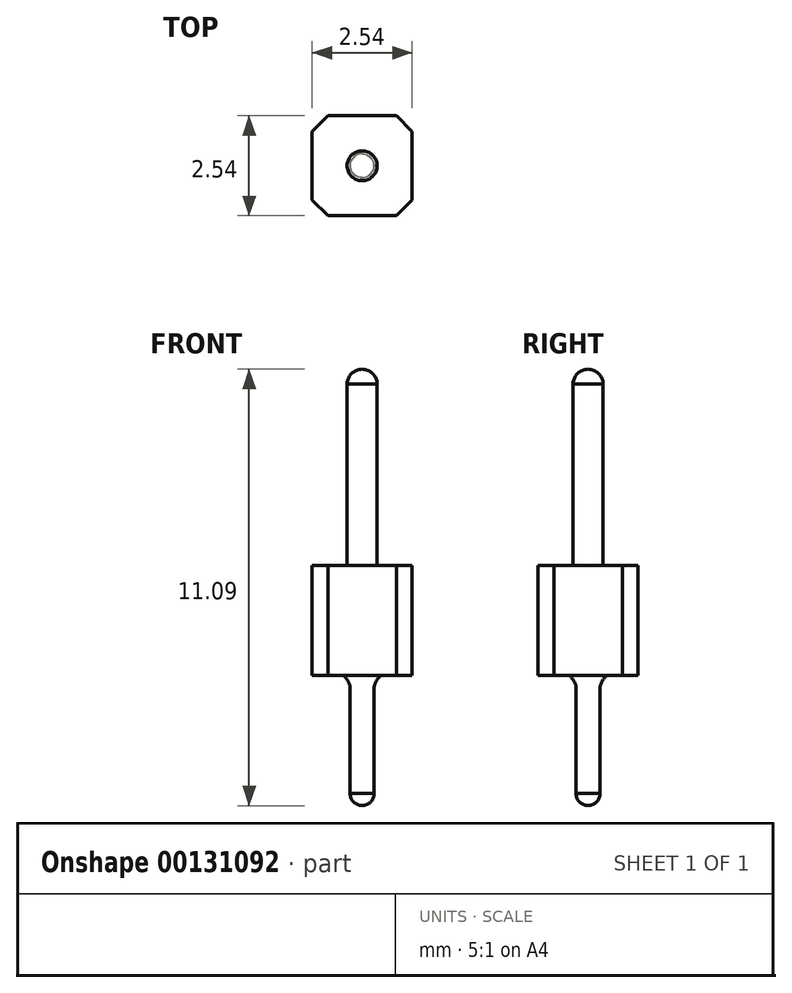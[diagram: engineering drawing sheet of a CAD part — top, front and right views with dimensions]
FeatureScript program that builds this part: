
annotation { "Feature Type Name" : "Feature", "Feature Type Description" : "" }
export const myFeature = defineFeature(function(context is Context, id is Id, definition is map)
    precondition{}
    {
        {
            var Q0;
            Q0=qCreatedBy(makeId("Top.planeOp"),FACE);
            var sketch = newSketch(context, id + "F0", { "sketchPlane" : qUnion([Q0])});
            skLineSegment(sketch, "E0", {"start": v(0, 0) * mm, "end": v(-1.27, 0) * mm});
            skCircle(sketch, "E1", {"center": v(-1.27, 0) * mm, "radius": 0.3 * mm});
            skSolve(sketch);
        }
        {
            var Q0;
            Q0=makeQuery(id+"F0.imprint","IMPRINT",FACE,{"disambiguationData":[TD([[makeQuery(id+"F0.imprint","IMPRINT",EDGE,{"derivedFrom":sQuery(id+"F0.wireOp",EDGE,"E1")}),1.0]])]});
            extrude(context, id + "F1", {"entities" : qUnion([Q0]), "oppositeDirection" : true, "depth" : 11.1 * mm, "hasSecondDirection" : true, "secondDirectionOppositeDirection" : true, "secondDirectionDepth" : 7.8 * mm});
        }
        {
            var Q0;
            Q0=makeQuery(id+"F1.opExtrude","CAP_FACE",FACE,{"disambiguationData":[OSD([sQuery(id+"F0.wireOp",EDGE,"E1")])],"isStart":false});
            extrude(context, id + "F2", {"entities" : qUnion([Q0]), "operationType" : NewBodyOperationType.REMOVE, "oppositeDirection" : true, "depth" : 0.3 * mm});
        }
        {
            var Q0;
            Q0=qCreatedBy(makeId("Top.planeOp"),FACE);
            var sketch = newSketch(context, id + "F3", { "sketchPlane" : qUnion([Q0])});
            skLineSegment(sketch, "E2", {"start": v(0, 0) * mm, "end": v(-1.27, 0) * mm});
            skCircle(sketch, "E3", {"center": v(-1.27, 0) * mm, "radius": 0.3 * mm});
            skLineSegment(sketch, "E4", {"start": v(-1.27, 0) * mm, "end": v(-1.8, 0) * mm});
            skSolve(sketch);
        }
        {
            var Q0;
            {var subQ0=sQuery(id+"F3.wireOp",EDGE,"E4");var subQ1=sQuery(id+"F3.wireOp",EDGE,"E2");var subQ2=makeQuery(id+"F3.imprint","INTERSECT",VERTEX,{"derivedFrom":[subQ1,subQ0]});Q0=makeQuery(id+"F3.imprint","IMPRINT",FACE,{"disambiguationData":[TD([[makeQuery(id+"F3.imprint","IMPRINT",EDGE,{"disambiguationData":[TD([[subQ2,1.0]])],"derivedFrom":subQ1}),-1.0]])]});}
            var Q1;
            Q1=sQuery(id+"F3.wireOp",EDGE,"E4");
            revolve(context, id + "F4", {"entities" : qUnion([Q0]), "axis" : qUnion([Q1]), "revolveType" : RevolveType.ONE_DIRECTION, "angle" : 180 * degree});
        }
        {
            var Q0;
            Q0=makeQuery(id+"F4.opRevolve","SWEPT_BODY",BODY,{"disambiguationData":[OSD([sQuery(id+"F3.wireOp",EDGE,"E2"),sQuery(id+"F3.wireOp",EDGE,"E3"),sQuery(id+"F3.wireOp",EDGE,"E4")])]});
            transform(context, id + "F5", {"entities" : qUnion([Q0]), "transformType" : TransformType.TRANSLATION_3D, "dx" : 0 * mm, "dy" : 0 * mm, "dz" : -10.8 * mm, "makeCopy" : false});
        }
        {
            var Q0;
            Q0=qCreatedBy(makeId("Top.planeOp"),FACE);
            var sketch = newSketch(context, id + "F6", { "sketchPlane" : qUnion([Q0])});
            skLineSegment(sketch, "E5", {"start": v(0, 0) * mm, "end": v(-1.27, 0) * mm});
            skLineSegment(sketch, "E6.bottom", {"start": v(0, 1.27) * mm, "end": v(-2.54, 1.27) * mm});
            skLineSegment(sketch, "E6.top", {"start": v(0, -1.27) * mm, "end": v(-2.54, -1.27) * mm});
            skLineSegment(sketch, "E6.left", {"start": v(0, 1.27) * mm, "end": v(0, -1.27) * mm});
            skLineSegment(sketch, "E6.right", {"start": v(-2.54, 1.27) * mm, "end": v(-2.54, -1.27) * mm});
            skPoint(sketch, "E6.middle", {"position": v(-1.27, 0) * mm});
            skSolve(sketch);
        }
        {
            var Q0;
            {var subQ3=sQuery(id+"F6.wireOp",EDGE,"E6.bottom");Q0=makeQuery(id+"F6.imprint","IMPRINT",FACE,{"disambiguationData":[TD([[makeQuery(id+"F6.imprint","IMPRINT",EDGE,{"derivedFrom":subQ3}),1.0]])]});}
            extrude(context, id + "F7", {"entities" : qUnion([Q0]), "oppositeDirection" : true, "depth" : 7.8 * mm, "hasSecondDirection" : true, "secondDirectionOppositeDirection" : true, "secondDirectionDepth" : 5 * mm});
        }
        {
            var Q0;
            Q0=qCreatedBy(makeId("Top.planeOp"),FACE);
            var sketch = newSketch(context, id + "F8", { "sketchPlane" : qUnion([Q0])});
            skLineSegment(sketch, "E7", {"start": v(0, 0) * mm, "end": v(-1.27, 0) * mm});
            skCircle(sketch, "E8", {"center": v(-1.27, 0) * mm, "radius": 0.38 * mm});
            skSolve(sketch);
        }
        {
            var Q0;
            Q0=makeQuery(id+"F8.imprint","IMPRINT",FACE,{"disambiguationData":[TD([[makeQuery(id+"F8.imprint","IMPRINT",EDGE,{"derivedFrom":sQuery(id+"F8.wireOp",EDGE,"E8")}),1.0]])]});
            extrude(context, id + "F9", {"entities" : qUnion([Q0]), "oppositeDirection" : true, "depth" : 5 * mm, "hasSecondDirection" : true, "secondDirectionOppositeDirection" : true, "secondDirectionDepth" : 0.4 * mm});
        }
        {
            var Q0;
            Q0=qCreatedBy(makeId("Top.planeOp"),FACE);
            var sketch = newSketch(context, id + "F10", { "sketchPlane" : qUnion([Q0])});
            skLineSegment(sketch, "E9", {"start": v(0, 0) * mm, "end": v(-1.27, 0) * mm});
            skCircle(sketch, "E10", {"center": v(-1.27, 0) * mm, "radius": 0.38 * mm});
            skLineSegment(sketch, "E11", {"start": v(-1.27, 0) * mm, "end": v(-1.76, 0) * mm});
            skSolve(sketch);
        }
        {
            var Q0;
            {var subQ0=sQuery(id+"F10.wireOp",EDGE,"E11");var subQ1=sQuery(id+"F10.wireOp",EDGE,"E9");var subQ2=makeQuery(id+"F10.imprint","INTERSECT",VERTEX,{"derivedFrom":[subQ1,subQ0]});Q0=makeQuery(id+"F10.imprint","IMPRINT",FACE,{"disambiguationData":[TD([[makeQuery(id+"F10.imprint","IMPRINT",EDGE,{"disambiguationData":[TD([[subQ2,1.0]])],"derivedFrom":subQ1}),-1.0]])]});}
            var Q1;
            Q1=sQuery(id+"F10.wireOp",EDGE,"E11");
            revolve(context, id + "F11", {"operationType" : NewBodyOperationType.ADD, "entities" : qUnion([Q0]), "axis" : qUnion([Q1]), "revolveType" : RevolveType.ONE_DIRECTION, "oppositeDirection" : true, "angle" : 180 * degree});
        }
        {
            var Q0;
            Q0=makeQuery(id+"F11.opRevolve","SWEPT_BODY",BODY,{"disambiguationData":[OSD([sQuery(id+"F10.wireOp",EDGE,"E9"),sQuery(id+"F10.wireOp",EDGE,"E10"),sQuery(id+"F10.wireOp",EDGE,"E11")])]});
            transform(context, id + "F12", {"entities" : qUnion([Q0]), "transformType" : TransformType.TRANSLATION_3D, "dx" : 0 * mm, "dy" : 0 * mm, "dz" : -0.4 * mm, "makeCopy" : false});
        }
        {
            var Q0;
            Q0=makeQuery(id+"F7.opExtrude","SWEPT_EDGE",EDGE,{"disambiguationData":[OSD([sQuery(id+"F6.wireOp",EDGE,"E6.top"),sQuery(id+"F6.wireOp",EDGE,"E6.right")])]});
            var Q1;
            Q1=makeQuery(id+"F7.opExtrude","SWEPT_EDGE",EDGE,{"disambiguationData":[OSD([sQuery(id+"F6.wireOp",EDGE,"E6.top"),sQuery(id+"F6.wireOp",EDGE,"E6.left")])]});
            var Q2;
            Q2=makeQuery(id+"F7.opExtrude","SWEPT_EDGE",EDGE,{"disambiguationData":[OSD([sQuery(id+"F6.wireOp",EDGE,"E6.bottom"),sQuery(id+"F6.wireOp",EDGE,"E6.left")])]});
            var Q3;
            Q3=makeQuery(id+"F7.opExtrude","SWEPT_EDGE",EDGE,{"disambiguationData":[OSD([sQuery(id+"F6.wireOp",EDGE,"E6.bottom"),sQuery(id+"F6.wireOp",EDGE,"E6.right")])]});
            chamfer(context, id + "F13", {"entities" : qUnion([Q0, Q1, Q2, Q3]), "width" : 0.4 * mm, "tangentPropagation" : true});
        }
        {
            var Q0;
            Q0=qCreatedBy(makeId("Top.planeOp"),FACE);
            cPlane(context, id + "F14", {"entities" : qUnion([Q0]), "cplaneType" : CPlaneType.OFFSET, "offset" : 7.8 * mm, "oppositeDirection" : true, "width" : 150 * mm, "height" : 150 * mm});
        }
        {
            var Q0;
            Q0=makeQuery(id+"F1.opExtrude","CAP_FACE",FACE,{"disambiguationData":[OSD([sQuery(id+"F0.wireOp",EDGE,"E1")])],"isStart":true});
            extrude(context, id + "F15", {"entities" : qUnion([Q0]), "operationType" : NewBodyOperationType.REMOVE, "oppositeDirection" : true, "depth" : 0.3 * mm});
        }
        {
            var Q0;
            Q0=qCreatedBy(id+"F14.planeOp",FACE);
            var sketch = newSketch(context, id + "F16", { "sketchPlane" : qUnion([Q0])});
            skLineSegment(sketch, "E12", {"start": v(0, 0) * mm, "end": v(-1.27, 0) * mm});
            skCircle(sketch, "E13", {"center": v(-1.27, 0) * mm, "radius": 0.5 * mm});
            skSolve(sketch);
        }
        {
            var Q1;
            Q1=makeQuery(id+"F15.boolean.opBoolean","COPY",FACE,{"derivedFrom":makeQuery(id+"F15.opExtrude","CAP_FACE",FACE,{"disambiguationData":[OSD([sQuery(id+"F0.wireOp",EDGE,"E1")])],"isStart":false})});
            var Q2;
            Q2=makeQuery(id+"F16.imprint","IMPRINT",FACE,{"disambiguationData":[TD([[makeQuery(id+"F16.imprint","IMPRINT",EDGE,{"derivedFrom":sQuery(id+"F16.wireOp",EDGE,"E13")}),1.0]])]});
            loft(context, id + "F17", {"operationType" : NewBodyOperationType.ADD, "startCondition" : LoftEndDerivativeType.NORMAL_TO_PROFILE, "startMagnitude" : 1, "endCondition" : LoftEndDerivativeType.TANGENT_TO_PROFILE, "endMagnitude" : 1, "sheetProfilesArray" : [{ "sheetProfileEntities" : qUnion([Q1]) }, { "sheetProfileEntities" : qUnion([Q2]) }]});
        }
    });
